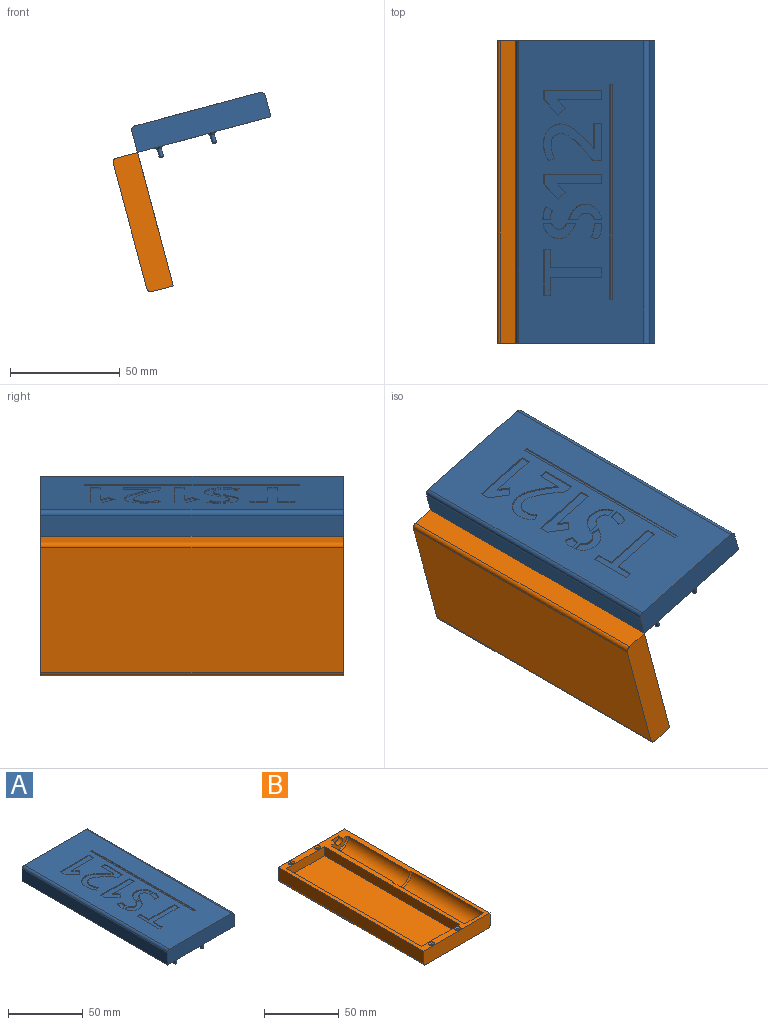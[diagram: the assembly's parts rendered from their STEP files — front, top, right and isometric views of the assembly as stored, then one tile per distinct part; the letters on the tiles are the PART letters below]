
ASSEMBLY  parts=2 mates=1
PART A: 152 faces, bbox 63x138x17 mm
  f0: plane 138x59mm, normal (0,0,1), area 7140.4mm2, adj f4,f5,f7,f8,f18,f19,f20,f21
  f1: plane 138.01x63.01mm, normal (0,0,-1), area 3889.8mm2, adj f2,f3,f6,f7,f8,f9,f10,f11
  f2: cylinder r=9mm len=133mm, axis (0,1,0), area 3656.4mm2, adj f1,f9,f10,f17
  f3: plane 138x10mm, normal (1,0,0), area 1380mm2, adj f1,f4,f7,f8
  f4: cylinder r=2mm len=138mm, axis (0,1,0), area 433.5mm2, adj f0,f3,f7,f8
  f5: cylinder r=2mm len=138mm, axis (0,1,0), area 433.5mm2, adj f0,f6,f7,f8
  f6: plane 138x10mm, normal (-1,0,0), area 1380mm2, adj f1,f5,f7,f8
  f7: plane 63x12mm, normal (0,-1,0), area 754.3mm2, adj f0,f1,f3,f4,f5,f6
  f8: plane 63x12mm, normal (0,1,0), area 754.3mm2, adj f0,f1,f3,f4,f5,f6
  f9: plane 18x9mm, normal (0,1,0), area 127.2mm2, adj f1,f2
  f10: plane 18x9mm, normal (0,-1,0), area 127.2mm2, adj f1,f2
  f11: plane 118x8mm, normal (-1,0,0), area 944mm2, adj f1,f12,f14,f15
  f12: plane 20x8mm, normal (0,1,0), area 160mm2, adj f1,f11,f13,f15
  f13: plane 118x8mm, normal (1,0,0), area 944mm2, adj f1,f12,f14,f15
  f14: plane 20x8mm, normal (0,-1,0), area 160mm2, adj f1,f11,f13,f15
  f15: plane 118x20mm, normal (0,0,-1), area 2360mm2, adj f11,f12,f13,f14
  f16: plane 11.17x7.19mm, normal (0,0,-1), area 61.8mm2, adj f17
  f17: bspline ~13.02x9.75mm, area 69.3mm2, adj f2,f16
  f18: plane 3.03x0.65mm, normal (0,-1,0), area 2mm2, adj f0,f19,f25,f26
  f19: plane 20.76x0.65mm, normal (1,0,0), area 13.5mm2, adj f0,f18,f20,f26
  f20: plane 3.03x0.65mm, normal (0,1,0), area 2mm2, adj f0,f19,f21,f26
  f21: plane 8.14x0.65mm, normal (-1,0,0), area 5.3mm2, adj f0,f20,f22,f26
  f22: plane 24.24x0.65mm, normal (0,1,0), area 15.8mm2, adj f0,f21,f23,f26
  f23: plane 4.48x0.65mm, normal (-1,0,0), area 2.9mm2, adj f0,f22,f24,f26
  f24: plane 24.24x0.65mm, normal (0,-1,0), area 15.8mm2, adj f0,f23,f25,f26
  f25: plane 8.14x0.65mm, normal (-1,0,0), area 5.3mm2, adj f0,f18,f24,f26
  f26: plane 27.28x20.76mm, normal (0,0,1), area 171.5mm2, adj f18,f19,f20,f21,f22,f23,f24,f25
  f27: plane 4.52x0.65mm, normal (-1,0,0), area 2.9mm2, adj f0,f28,f33,f34
  f28: plane 27.28x0.65mm, normal (0,-1,0), area 17.7mm2, adj f0,f27,f29,f34
  f29: plane 4.52x0.65mm, normal (1,0,0), area 2.9mm2, adj f0,f28,f30,f34
  f30: plane 6.92x6.92mm, normal (0.71,0.71,0), area 6.4mm2, adj f0,f29,f31,f34
  f31: plane 3.19x3.19mm, normal (-0.71,0.71,0), area 2.9mm2, adj f0,f30,f32,f34
  f32: plane 3.74x3.74mm, normal (-0.71,-0.71,0), area 3.4mm2, adj f0,f31,f33,f34
  f33: plane 20.91x0.65mm, normal (0,1,0), area 13.6mm2, adj f0,f27,f32,f34
  f34: plane 27.28x11.44mm, normal (0,0,1), area 157.2mm2, adj f27,f28,f29,f30,f31,f32,f33
  f35: extruded ~2.98x0.65mm, area 2mm2, adj f0,f36,f67,f68
  f36: extruded ~2.85x0.65mm, area 1.9mm2, adj f0,f35,f37,f68
  f37: extruded ~2.68x1.65mm, area 2.1mm2, adj f0,f36,f38,f68
  f38: extruded ~2.83x1.98mm, area 2.3mm2, adj f0,f37,f39,f68
  f39: extruded ~4.12x0.78mm, area 2.7mm2, adj f0,f38,f40,f68
  f40: extruded ~1.92x0.65mm, area 1.3mm2, adj f0,f39,f41,f68
  f41: extruded ~2.09x0.65mm, area 1.4mm2, adj f0,f40,f42,f68
  f42: extruded ~2.04x0.78mm, area 1.4mm2, adj f0,f41,f43,f68
  f43: extruded ~1.65x1.07mm, area 1.3mm2, adj f0,f42,f44,f68
  f44: plane 2.74x1.3mm, normal (-0.43,0.9,0), area 2mm2, adj f0,f43,f45,f68
  f45: extruded ~1.18x0.67mm, area 0.9mm2, adj f0,f44,f46,f68
  f46: extruded ~1.26x0.65mm, area 0.9mm2, adj f0,f45,f47,f68
  f47: extruded ~1.65x0.65mm, area 1.1mm2, adj f0,f46,f48,f68
  f48: extruded ~2.38x0.65mm, area 1.6mm2, adj f0,f47,f49,f68
  f49: extruded ~1.58x0.65mm, area 1mm2, adj f0,f48,f50,f68
  f50: extruded ~1.54x0.78mm, area 1.1mm2, adj f0,f49,f51,f68
  f51: extruded ~1.42x1.16mm, area 1.2mm2, adj f0,f50,f52,f68
  f52: extruded ~2.17x0.65mm, area 1.5mm2, adj f0,f51,f53,f68
  f53: extruded ~2.66x0.72mm, area 1.8mm2, adj f0,f52,f54,f68
  f54: extruded ~2.87x1.85mm, area 2.2mm2, adj f0,f53,f55,f68
  f55: extruded ~2.89x2.5mm, area 2.5mm2, adj f0,f54,f56,f68
  f56: extruded ~2.74x2.68mm, area 2.5mm2, adj f0,f55,f57,f68
  f57: extruded ~2.56x2.28mm, area 2.2mm2, adj f0,f56,f58,f68
  f58: extruded ~1.85x1.61mm, area 1.6mm2, adj f0,f57,f59,f68
  f59: plane 4.15x0.65mm, normal (0,1,0), area 2.7mm2, adj f0,f58,f60,f68
  f60: plane 16.95x0.65mm, normal (-1,0,0), area 11mm2, adj f0,f59,f61,f68
  f61: plane 3.59x0.65mm, normal (0,-1,0), area 2.3mm2, adj f0,f60,f62,f68
  f62: plane 11.58x0.65mm, normal (1,0,0), area 7.5mm2, adj f0,f61,f63,f68
  f63: extruded ~1.8x1.72mm, area 1.6mm2, adj f0,f62,f64,f68
  f64: extruded ~2.33x2.28mm, area 2.1mm2, adj f0,f63,f65,f68
  f65: extruded ~2.67x2.48mm, area 2.4mm2, adj f0,f64,f66,f68
  f66: extruded ~2.9x2.28mm, area 2.4mm2, adj f0,f65,f67,f68
  f67: extruded ~3.04x1.67mm, area 2.3mm2, adj f0,f35,f66,f68
  f68: plane 27.47x17.24mm, normal (0,0,1), area 208.8mm2, adj f35,f36,f37,f38,f39,f40,f41,f42
  f69: plane 4.52x0.65mm, normal (-1,0,0), area 2.9mm2, adj f0,f70,f75,f76
  f70: plane 27.28x0.65mm, normal (0,-1,0), area 17.7mm2, adj f0,f69,f71,f76
  f71: plane 4.52x0.65mm, normal (1,0,0), area 2.9mm2, adj f0,f70,f72,f76
  f72: plane 6.92x6.92mm, normal (0.71,0.71,0), area 6.4mm2, adj f0,f71,f73,f76
  f73: plane 3.19x3.19mm, normal (-0.71,0.71,0), area 2.9mm2, adj f0,f72,f74,f76
  f74: plane 3.74x3.74mm, normal (-0.71,-0.71,0), area 3.4mm2, adj f0,f73,f75,f76
  f75: plane 20.91x0.65mm, normal (0,1,0), area 13.6mm2, adj f0,f69,f74,f76
  f76: plane 27.28x11.44mm, normal (0,0,1), area 157.2mm2, adj f69,f70,f71,f72,f73,f74,f75
  f77: plane 98x0.65mm, normal (1,0,0), area 63.7mm2, adj f0,f78,f80,f81
  f78: plane 1.33x0.65mm, normal (0,1,0), area 0.9mm2, adj f0,f77,f79,f81
  f79: plane 98x0.65mm, normal (-1,0,0), area 63.7mm2, adj f0,f78,f80,f81
  f80: plane 1.33x0.65mm, normal (0,-1,0), area 0.9mm2, adj f0,f77,f79,f81
  f81: plane 98x1.33mm, normal (0,0,1), area 130.8mm2, adj f77,f78,f79,f80
  f82: extruded ~0.65x0.44mm, area 0.3mm2, adj f0,f83,f92,f93
  f83: extruded ~0.65x0.37mm, area 0.3mm2, adj f0,f82,f84,f93
  f84: extruded ~0.83x0.65mm, area 0.6mm2, adj f0,f83,f85,f93
  f85: extruded ~1.07x0.65mm, area 0.8mm2, adj f0,f84,f86,f93
  f86: extruded ~1.05x0.65mm, area 0.8mm2, adj f0,f85,f87,f93
  f87: extruded ~2.72x0.98mm, area 1.9mm2, adj f0,f86,f88,f93
  f88: extruded ~3.31x0.65mm, area 2.2mm2, adj f0,f87,f89,f93
  f89: plane 3.74x0.65mm, normal (0,1,0), area 2.4mm2, adj f0,f88,f90,f93
  f90: extruded ~1.89x0.65mm, area 1.2mm2, adj f0,f89,f91,f93
  f91: extruded ~1.22x0.65mm, area 0.8mm2, adj f0,f90,f92,f93
  f92: extruded ~0.74x0.65mm, area 0.5mm2, adj f0,f82,f91,f93
  f93: plane 6.03x4.66mm, normal (0,0,1), area 19.8mm2, adj f82,f83,f84,f85,f86,f87,f88,f89
  f94: extruded ~2.92x0.65mm, area 1.9mm2, adj f0,f95,f107,f108
  f95: extruded ~2.93x0.65mm, area 2mm2, adj f0,f94,f96,f108
  f96: extruded ~2.15x1.65mm, area 1.8mm2, adj f0,f95,f97,f108
  f97: extruded ~2.22x1.61mm, area 1.8mm2, adj f0,f96,f98,f108
  f98: extruded ~2.45x1.28mm, area 1.8mm2, adj f0,f97,f99,f108
  f99: plane 4.22x0.65mm, normal (0,-1,0), area 2.7mm2, adj f0,f98,f100,f108
  f100: extruded ~1.96x1.55mm, area 1.6mm2, adj f0,f99,f101,f108
  f101: extruded ~2.33x0.78mm, area 1.6mm2, adj f0,f100,f102,f108
  f102: extruded ~2.06x0.78mm, area 1.5mm2, adj f0,f101,f103,f108
  f103: extruded ~1.96x1.42mm, area 1.6mm2, adj f0,f102,f104,f108
  f104: plane 3.89x0.65mm, normal (0,-1,0), area 2.5mm2, adj f0,f103,f105,f108
  f105: extruded ~2.69x0.76mm, area 1.8mm2, adj f0,f104,f106,f108
  f106: extruded ~2.22x1.55mm, area 1.8mm2, adj f0,f105,f107,f108
  f107: extruded ~2.28x1.5mm, area 1.8mm2, adj f0,f94,f106,f108
  f108: plane 15.47x6.96mm, normal (0,0,1), area 65.2mm2, adj f94,f95,f96,f97,f98,f99,f100,f101
  f109: extruded ~1.31x0.65mm, area 0.9mm2, adj f0,f110,f120,f121
  f110: plane 3.19x0.78mm, normal (0.24,0.97,0), area 2.1mm2, adj f0,f109,f111,f121
  f111: extruded ~1.5x0.94mm, area 1.2mm2, adj f0,f110,f112,f121
  f112: extruded ~1.83x0.65mm, area 1.3mm2, adj f0,f111,f113,f121
  f113: extruded ~1.91x0.65mm, area 1.3mm2, adj f0,f112,f114,f121
  f114: extruded ~1.83x0.65mm, area 1.2mm2, adj f0,f113,f115,f121
  f115: plane 0.65x0.08mm, normal (-1,0,0), area 0.1mm2, adj f0,f114,f116,f121
  f116: plane 3.52x0.65mm, normal (0,-1,0), area 2.3mm2, adj f0,f115,f117,f121
  f117: plane 0.65x0.11mm, normal (1,0,0), area 0.1mm2, adj f0,f116,f118,f121
  f118: extruded ~1.59x0.65mm, area 1mm2, adj f0,f117,f119,f121
  f119: extruded ~1.7x0.65mm, area 1.1mm2, adj f0,f118,f120,f121
  f120: extruded ~1.65x0.65mm, area 1.1mm2, adj f0,f109,f119,f121
  f121: plane 7.15x5.15mm, normal (0,0,1), area 24.9mm2, adj f109,f110,f111,f112,f113,f114,f115,f116
  f122: extruded ~2.5x1.19mm, area 1.8mm2, adj f0,f123,f134,f135
  f123: plane 4.33x0.65mm, normal (0,1,0), area 2.8mm2, adj f0,f122,f124,f135
  f124: extruded ~2.18x1.59mm, area 1.8mm2, adj f0,f123,f125,f135
  f125: extruded ~2.15x0.85mm, area 1.5mm2, adj f0,f124,f126,f135
  f126: extruded ~4.03x3.03mm, area 3.6mm2, adj f0,f125,f127,f135
  f127: plane 3.55x0.65mm, normal (0,1,0), area 2.3mm2, adj f0,f126,f128,f135
  f128: extruded ~3.03x0.92mm, area 2.1mm2, adj f0,f127,f129,f135
  f129: extruded ~2.24x1.72mm, area 1.8mm2, adj f0,f128,f130,f135
  f130: extruded ~2.28x1.41mm, area 1.7mm2, adj f0,f129,f131,f135
  f131: extruded ~2.59x0.65mm, area 1.7mm2, adj f0,f130,f132,f135
  f132: extruded ~3.22x0.67mm, area 2.2mm2, adj f0,f131,f133,f135
  f133: extruded ~2.2x1.7mm, area 1.8mm2, adj f0,f132,f134,f135
  f134: extruded ~2.31x1.54mm, area 1.8mm2, adj f0,f122,f133,f135
  f135: plane 15.66x7.18mm, normal (0,0,1), area 66.2mm2, adj f122,f123,f124,f125,f126,f127,f128,f129
  f136: cylinder r=1mm len=3.6mm, axis (0,0,1), area 22.6mm2, adj f147,f151
  f137: plane 1.2x1.2mm, normal (0,0,-1), area 1.1mm2, adj f151
  f138: cylinder r=1mm len=3.6mm, axis (0,0,1), area 22.6mm2, adj f146,f150
  f139: plane 1.2x1.2mm, normal (0,0,-1), area 1.1mm2, adj f150
  f140: cylinder r=1mm len=3.6mm, axis (0,0,1), area 22.6mm2, adj f145,f148
  f141: plane 1.2x1.2mm, normal (0,0,-1), area 1.1mm2, adj f148
  f142: cylinder r=1mm len=3.6mm, axis (0,0,1), area 22.6mm2, adj f144,f149
  f143: plane 1.2x1.2mm, normal (0,0,-1), area 1.1mm2, adj f149
  f144: bspline ~4x4mm, area 13.1mm2, adj f1,f142
  f145: bspline ~4x4mm, area 13.1mm2, adj f1,f140
  f146: bspline ~4x4mm, area 13.1mm2, adj f1,f138
  f147: bspline ~4x4mm, area 13.1mm2, adj f1,f136
  f148: cone r=0.6mm half-angle=45deg, axis (0,0,1), area 2.8mm2, adj f140,f141
  f149: cone r=0.6mm half-angle=45deg, axis (0,0,1), area 2.8mm2, adj f142,f143
  f150: cone r=0.6mm half-angle=45deg, axis (0,0,1), area 2.8mm2, adj f138,f139
  f151: cone r=0.6mm half-angle=45deg, axis (0,0,1), area 2.8mm2, adj f136,f137
PART B: 33 faces, bbox 63x138x12 mm
  f0: plane 138.01x63.01mm, normal (0,0,1), area 1815.1mm2, adj f1,f2,f6,f7,f8,f9,f10,f11
  f1: cylinder r=9mm len=68mm, axis (0,1,0), area 1922.7mm2, adj f0,f12,f15
  f2: plane 138x10mm, normal (-1,0,0), area 1380mm2, adj f0,f3,f11,f13
  f3: cylinder r=2mm len=138mm, axis (0,1,0), area 433.5mm2, adj f2,f4,f11,f13
  f4: plane 138x59mm, normal (0,0,-1), area 8142mm2, adj f3,f5,f11,f13
  f5: cylinder r=2mm len=138mm, axis (0,1,0), area 433.5mm2, adj f4,f6,f11,f13
  f6: plane 138x10mm, normal (1,0,0), area 1380mm2, adj f0,f5,f11,f13
  f7: cylinder r=8mm len=58mm, axis (0,-1,0), area 1457.7mm2, adj f0,f14,f15
  f8: plane 14x7mm, normal (0,-1,0), area 56.6mm2, adj f0,f9,f14
  f9: cylinder r=3.6mm len=7.2mm, axis (0,-1,0), area 45.2mm2, adj f0,f8,f10
  f10: plane 7.2x3.6mm, normal (0,-1,0), area 20.4mm2, adj f0,f9
  f11: plane 63x12mm, normal (0,1,0), area 754.3mm2, adj f0,f2,f3,f4,f5,f6
  f12: plane 18x9mm, normal (0,1,0), area 127.2mm2, adj f0,f1
  f13: plane 63x12mm, normal (0,-1,0), area 754.3mm2, adj f0,f2,f3,f4,f5,f6
  f14: cone r=7mm half-angle=45deg, axis (0,-1,0), area 33.3mm2, adj f0,f7,f8
  f15: cone r=8mm half-angle=45deg, axis (0,-1,0), area 37.8mm2, adj f0,f1,f7
  f16: plane 128x7.5mm, normal (1,0,0), area 960mm2, adj f0,f17,f19,f20
  f17: plane 36x7.5mm, normal (0,1,0), area 270mm2, adj f0,f16,f18,f20
  f18: plane 128x7.5mm, normal (-1,0,0), area 960mm2, adj f0,f17,f19,f20
  f19: plane 36x7.5mm, normal (0,-1,0), area 270mm2, adj f0,f16,f18,f20
  f20: plane 128x36mm, normal (0,0,1), area 4608mm2, adj f16,f17,f18,f19
  f21: cylinder r=1.15mm len=5mm, axis (0,0,1), area 36.1mm2, adj f22,f32
  f22: plane 2.3x2.3mm, normal (0,0,1), area 4.2mm2, adj f21
  f23: cylinder r=1.15mm len=5mm, axis (0,0,1), area 36.1mm2, adj f24,f29
  f24: plane 2.3x2.3mm, normal (0,0,1), area 4.2mm2, adj f23
  f25: cylinder r=1.15mm len=5mm, axis (0,0,1), area 36.1mm2, adj f26,f30
  f26: plane 2.3x2.3mm, normal (0,0,1), area 4.2mm2, adj f25
  f27: cylinder r=1.15mm len=5mm, axis (0,0,1), area 36.1mm2, adj f28,f31
  f28: plane 2.3x2.3mm, normal (0,0,1), area 4.2mm2, adj f27
  f29: bspline ~4.3x4.3mm, area 14.5mm2, adj f0,f23
  f30: bspline ~4.3x4.3mm, area 14.5mm2, adj f0,f25
  f31: bspline ~4.3x4.3mm, area 14.5mm2, adj f0,f27
  f32: bspline ~4.3x4.3mm, area 14.5mm2, adj f0,f21
PLACE A rot(axis=(0,-1,0),15deg) t=(28.32,30.42,32.35)mm
PLACE B rot(axis=(0,1,0),75deg) t=(-7.74,30.42,-30.12)mm
MATE fastened B.f2 <-> A.f1  axis (-0.26,0,0.97) through (-20.94,-40.58,19.15)mm
